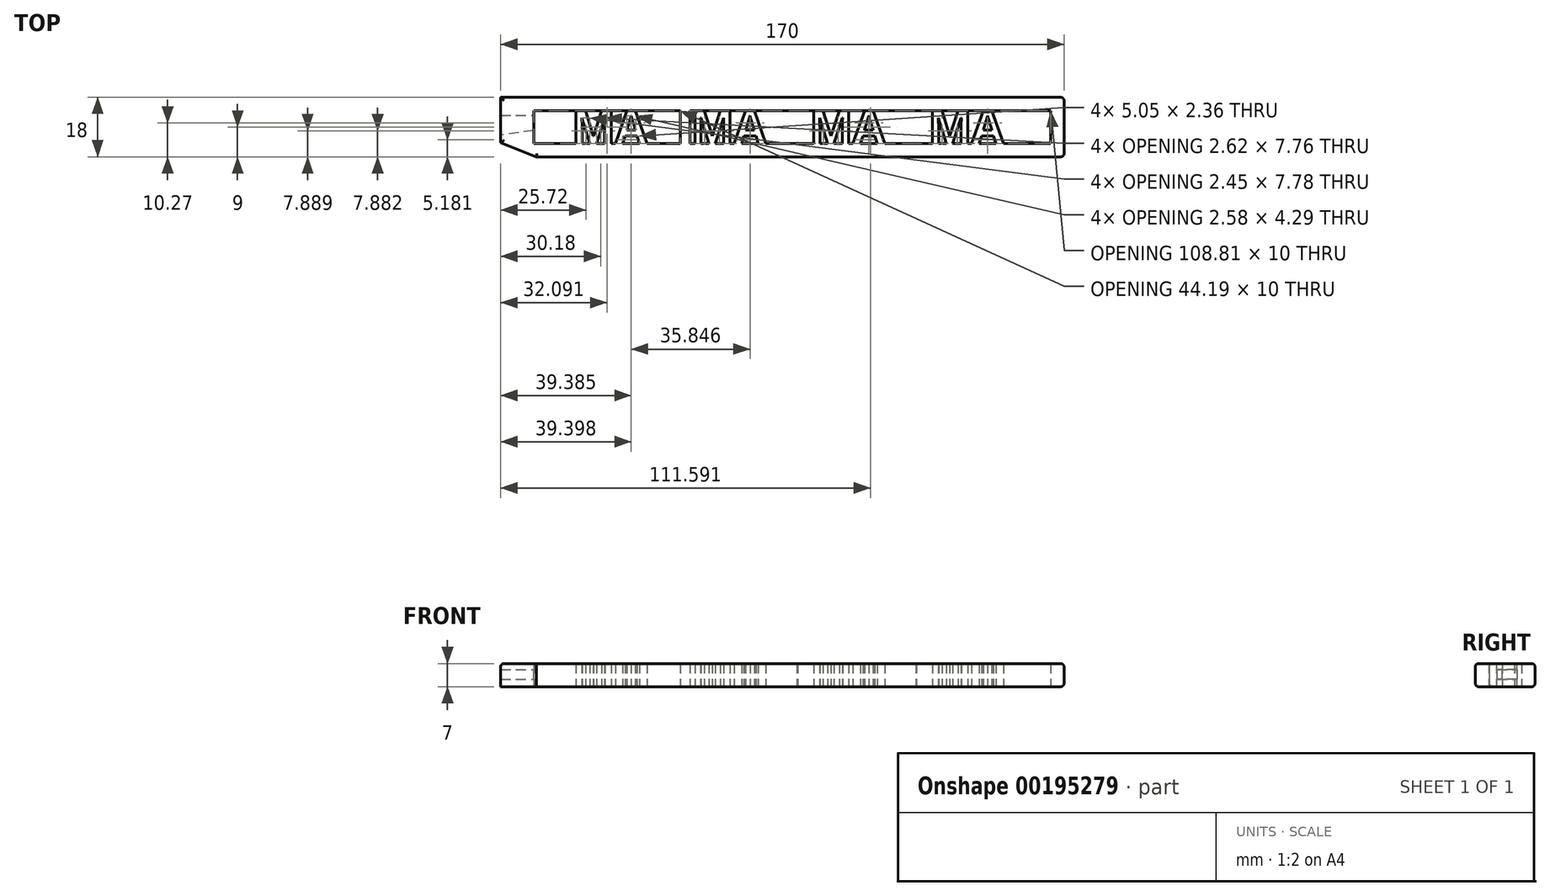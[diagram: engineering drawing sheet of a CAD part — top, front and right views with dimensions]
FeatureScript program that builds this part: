
annotation { "Feature Type Name" : "Feature", "Feature Type Description" : "" }
export const myFeature = defineFeature(function(context is Context, id is Id, definition is map)
    precondition{}
    {
        {
            var Q0;
            Q0=qCreatedBy(makeId("Top.planeOp"),FACE);
            var sketch = newSketch(context, id + "F0", { "sketchPlane" : qUnion([Q0])});
            skLineSegment(sketch, "E0.bottom", {"start": v(54.29, -9) * mm, "end": v(-115.71, -9) * mm});
            skLineSegment(sketch, "E0.top", {"start": v(54.29, 9) * mm, "end": v(-115.71, 9) * mm});
            skLineSegment(sketch, "E0.left", {"start": v(54.29, -9) * mm, "end": v(54.29, 9) * mm});
            skLineSegment(sketch, "E0.right", {"start": v(-115.71, -9) * mm, "end": v(-115.71, 9) * mm});
            skLineSegment(sketch, "E1.bottom", {"start": v(-105.71, 5) * mm, "end": v(50.29, 5) * mm});
            skLineSegment(sketch, "E1.top", {"start": v(-105.71, -5) * mm, "end": v(50.29, -5) * mm});
            skLineSegment(sketch, "E1.left", {"start": v(-105.71, 5) * mm, "end": v(-105.71, -5) * mm});
            skLineSegment(sketch, "E1.right", {"start": v(50.29, 5) * mm, "end": v(50.29, -5) * mm});
            skText(sketch, "E2", { "text": " MAX MAX MAX MAX ", "fontName": "OpenSans-Bold.ttf"});
            skLineSegment(sketch, "E3", {"start": v(-26.27, 5) * mm, "end": v(-26.27, -5) * mm});
            skLineSegment(sketch, "E4", {"start": v(-23.27, -5) * mm, "end": v(-23.27, 5) * mm});
            skLineSegment(sketch, "E5", {"start": v(9.6, 5) * mm, "end": v(9.6, -5) * mm});
            skLineSegment(sketch, "E6", {"start": v(12.6, 5) * mm, "end": v(12.6, -5) * mm});
            skLineSegment(sketch, "E7", {"start": v(-61.52, 5) * mm, "end": v(-61.52, -5) * mm});
            skLineSegment(sketch, "E8", {"start": v(-58.52, -5) * mm, "end": v(-58.52, 5) * mm});
            skPoint(sketch, "E9", {"position": v(-57.42, -2.4) * mm});
            skPoint(sketch, "E10", {"position": v(13.7, -2.4) * mm});
            const initialGuessF0  = {"E2": [-0.09782, -0.005, 1, 0, 0.01]};
            skSetInitialGuess(sketch, initialGuessF0);
            skSolve(sketch);
        }
        {
            var Q0;
            Q0=makeQuery(id+"F0.imprint","IMPRINT",FACE,{"disambiguationData":[TD([[makeQuery(id+"F0.imprint","IMPRINT",EDGE,{"derivedFrom":sQuery(id+"F0.wireOp",EDGE,"E0.bottom")}),-1.0]])]});
            var Q1;
            Q1=makeQuery(id+"F0.imprint","IMPRINT",FACE,{"disambiguationData":[TD([[makeQuery(id+"F0.imprint","IMPRINT",EDGE,{"derivedFrom":sQuery(id+"F0.wireOp",EDGE,"E2.sketch_text.stroke-0")}),-1.0]])]});
            var Q2;
            Q2=makeQuery(id+"F0.imprint","IMPRINT",FACE,{"disambiguationData":[TD([[makeQuery(id+"F0.imprint","IMPRINT",EDGE,{"derivedFrom":sQuery(id+"F0.wireOp",EDGE,"E2.sketch_text.stroke-19")}),-1.0]])]});
            var Q3;
            Q3=makeQuery(id+"F0.imprint","IMPRINT",FACE,{"disambiguationData":[TD([[makeQuery(id+"F0.imprint","IMPRINT",EDGE,{"derivedFrom":sQuery(id+"F0.wireOp",EDGE,"E2.sketch_text.stroke-31")}),-1.0]])]});
            var Q4;
            Q4=makeQuery(id+"F0.imprint","IMPRINT",FACE,{"disambiguationData":[TD([[makeQuery(id+"F0.imprint","IMPRINT",EDGE,{"derivedFrom":sQuery(id+"F0.wireOp",EDGE,"E2.sketch_text.stroke-43")}),-1.0]])]});
            var Q5;
            Q5=makeQuery(id+"F0.imprint","IMPRINT",FACE,{"disambiguationData":[TD([[makeQuery(id+"F0.imprint","IMPRINT",EDGE,{"derivedFrom":sQuery(id+"F0.wireOp",EDGE,"E2.sketch_text.stroke-62")}),-1.0]])]});
            var Q6;
            Q6=makeQuery(id+"F0.imprint","IMPRINT",FACE,{"disambiguationData":[TD([[makeQuery(id+"F0.imprint","IMPRINT",EDGE,{"derivedFrom":sQuery(id+"F0.wireOp",EDGE,"E2.sketch_text.stroke-74")}),-1.0]])]});
            var Q7;
            Q7=makeQuery(id+"F0.imprint","IMPRINT",FACE,{"disambiguationData":[TD([[makeQuery(id+"F0.imprint","IMPRINT",EDGE,{"derivedFrom":sQuery(id+"F0.wireOp",EDGE,"E2.sketch_text.stroke-86")}),-1.0]])]});
            var Q8;
            Q8=makeQuery(id+"F0.imprint","IMPRINT",FACE,{"disambiguationData":[TD([[makeQuery(id+"F0.imprint","IMPRINT",EDGE,{"derivedFrom":sQuery(id+"F0.wireOp",EDGE,"E2.sketch_text.stroke-105")}),-1.0]])]});
            var Q9;
            Q9=makeQuery(id+"F0.imprint","IMPRINT",FACE,{"disambiguationData":[TD([[makeQuery(id+"F0.imprint","IMPRINT",EDGE,{"derivedFrom":sQuery(id+"F0.wireOp",EDGE,"E2.sketch_text.stroke-117")}),-1.0]])]});
            var Q10;
            Q10=makeQuery(id+"F0.imprint","IMPRINT",FACE,{"disambiguationData":[TD([[makeQuery(id+"F0.imprint","IMPRINT",EDGE,{"derivedFrom":sQuery(id+"F0.wireOp",EDGE,"E2.sketch_text.stroke-129")}),-1.0]])]});
            var Q11;
            Q11=makeQuery(id+"F0.imprint","IMPRINT",FACE,{"disambiguationData":[TD([[makeQuery(id+"F0.imprint","IMPRINT",EDGE,{"derivedFrom":sQuery(id+"F0.wireOp",EDGE,"E2.sketch_text.stroke-148")}),-1.0]])]});
            var Q12;
            Q12=makeQuery(id+"F0.imprint","IMPRINT",FACE,{"disambiguationData":[TD([[makeQuery(id+"F0.imprint","IMPRINT",EDGE,{"derivedFrom":sQuery(id+"F0.wireOp",EDGE,"E2.sketch_text.stroke-160")}),-1.0]])]});
            var Q13;
            {var subQ0=sQuery(id+"F0.wireOp",EDGE,"E7");Q13=makeQuery(id+"F0.imprint","IMPRINT",FACE,{"disambiguationData":[TD([[makeQuery(id+"F0.imprint","IMPRINT",EDGE,{"derivedFrom":subQ0}),1.0]])]});}
            var Q14;
            {var subQ0=sQuery(id+"F0.wireOp",EDGE,"E3");Q14=makeQuery(id+"F0.imprint","IMPRINT",FACE,{"disambiguationData":[TD([[makeQuery(id+"F0.imprint","IMPRINT",EDGE,{"derivedFrom":subQ0}),1.0]])]});}
            var Q15;
            {var subQ0=sQuery(id+"F0.wireOp",EDGE,"E5");Q15=makeQuery(id+"F0.imprint","IMPRINT",FACE,{"disambiguationData":[TD([[makeQuery(id+"F0.imprint","IMPRINT",EDGE,{"derivedFrom":subQ0}),1.0]])]});}
            extrude(context, id + "F1", {"entities" : qUnion([Q0, Q1, Q2, Q3, Q4, Q5, Q6, Q7, Q8, Q9, Q10, Q11, Q12, Q13, Q14, Q15]), "endBound" : BoundingType.SYMMETRIC, "depth" : 7 * mm});
        }
        {
            var Q0;
            Q0=qCreatedBy(makeId("Top.planeOp"),FACE);
            var sketch = newSketch(context, id + "F2", { "sketchPlane" : qUnion([Q0])});
            skLineSegment(sketch, "E11", {"start": v(-116.71, 3.5) * mm, "end": v(-105.21, 3.5) * mm});
            skLineSegment(sketch, "E12", {"start": v(-105.21, -1) * mm, "end": v(-116.71, -2.5) * mm});
            skLineSegment(sketch, "E13", {"start": v(-105.21, 3.5) * mm, "end": v(-105.21, -1) * mm});
            skLineSegment(sketch, "E14", {"start": v(-116.71, 3.5) * mm, "end": v(-116.71, -2.5) * mm});
            skSolve(sketch);
        }
        {
            var Q0;
            Q0 = qSketchRegion(id + "F2", true);
            extrude(context, id + "F3", {"entities" : qUnion([Q0]), "operationType" : NewBodyOperationType.REMOVE, "depth" : 1.7 * mm, "hasSecondDirection" : true, "secondDirectionOppositeDirection" : true, "secondDirectionDepth" : 1.2 * mm});
        }
        {
            var Q0;
            Q0=qCreatedBy(makeId("Top.planeOp"),FACE);
            var sketch = newSketch(context, id + "F4", { "sketchPlane" : qUnion([Q0])});
            skLineSegment(sketch, "E15", {"start": v(-104.42, -9.2) * mm, "end": v(-117.77, -3.9) * mm});
            skLineSegment(sketch, "E16", {"start": v(-117.77, -3.9) * mm, "end": v(-117.77, -10.56) * mm});
            skLineSegment(sketch, "E17", {"start": v(-117.77, -10.56) * mm, "end": v(-104.42, -9.2) * mm});
            skSolve(sketch);
        }
        {
            var Q0;
            Q0 = qSketchRegion(id + "F4", true);
            extrude(context, id + "F5", {"entities" : qUnion([Q0]), "operationType" : NewBodyOperationType.REMOVE, "endBound" : BoundingType.SYMMETRIC, "depth" : 15 * mm});
        }
        {
            var Q0;
            Q0=makeQuery(id+"F1.opExtrude","CAP_EDGE",EDGE,{"disambiguationData":[OSD([sQuery(id+"F0.wireOp",EDGE,"E0.left")])],"isStart":true});
            var Q1;
            Q1=makeQuery(id+"F1.opExtrude","CAP_EDGE",EDGE,{"disambiguationData":[OSD([sQuery(id+"F0.wireOp",EDGE,"E0.top")])],"isStart":true});
            var Q2;
            Q2=makeQuery(id+"F1.opExtrude","CAP_EDGE",EDGE,{"disambiguationData":[OSD([sQuery(id+"F0.wireOp",EDGE,"E0.bottom")])],"isStart":true});
            var Q3;
            Q3=makeQuery(id+"F1.opExtrude","CAP_EDGE",EDGE,{"disambiguationData":[OSD([sQuery(id+"F0.wireOp",EDGE,"E0.left")])],"isStart":false});
            var Q4;
            Q4=makeQuery(id+"F1.opExtrude","SWEPT_EDGE",EDGE,{"disambiguationData":[OSD([sQuery(id+"F0.wireOp",EDGE,"E0.top"),sQuery(id+"F0.wireOp",EDGE,"E0.left")])]});
            var Q5;
            Q5=makeQuery(id+"F1.opExtrude","SWEPT_EDGE",EDGE,{"disambiguationData":[OSD([sQuery(id+"F0.wireOp",EDGE,"E0.bottom"),sQuery(id+"F0.wireOp",EDGE,"E0.left")])]});
            var Q6;
            Q6=makeQuery(id+"F5.boolean.opBoolean","INTERSECT",EDGE,{"derivedFrom":[makeQuery(id+"F1.opExtrude","CAP_FACE",FACE,{"disambiguationData":[OSD([sQuery(id+"F0.wireOp",EDGE,"E0.bottom"),sQuery(id+"F0.wireOp",EDGE,"E0.top"),sQuery(id+"F0.wireOp",EDGE,"E0.left"),sQuery(id+"F0.wireOp",EDGE,"E0.right"),sQuery(id+"F0.wireOp",EDGE,"E1.bottom"),sQuery(id+"F0.wireOp",EDGE,"E1.top"),sQuery(id+"F0.wireOp",EDGE,"E1.left"),sQuery(id+"F0.wireOp",EDGE,"E1.right"),sQuery(id+"F0.wireOp",EDGE,"E2.sketch_text.stroke-0"),sQuery(id+"F0.wireOp",EDGE,"E2.sketch_text.stroke-1"),sQuery(id+"F0.wireOp",EDGE,"E2.sketch_text.stroke-2"),sQuery(id+"F0.wireOp",EDGE,"E2.sketch_text.stroke-3"),sQuery(id+"F0.wireOp",EDGE,"E2.sketch_text.stroke-5"),sQuery(id+"F0.wireOp",EDGE,"E2.sketch_text.stroke-6"),sQuery(id+"F0.wireOp",EDGE,"E2.sketch_text.stroke-7"),sQuery(id+"F0.wireOp",EDGE,"E2.sketch_text.stroke-8"),sQuery(id+"F0.wireOp",EDGE,"E2.sketch_text.stroke-9"),sQuery(id+"F0.wireOp",EDGE,"E2.sketch_text.stroke-10"),sQuery(id+"F0.wireOp",EDGE,"E2.sketch_text.stroke-11"),sQuery(id+"F0.wireOp",EDGE,"E2.sketch_text.stroke-13"),sQuery(id+"F0.wireOp",EDGE,"E2.sketch_text.stroke-14"),sQuery(id+"F0.wireOp",EDGE,"E2.sketch_text.stroke-15"),sQuery(id+"F0.wireOp",EDGE,"E2.sketch_text.stroke-16"),sQuery(id+"F0.wireOp",EDGE,"E2.sketch_text.stroke-17"),sQuery(id+"F0.wireOp",EDGE,"E2.sketch_text.stroke-19"),sQuery(id+"F0.wireOp",EDGE,"E2.sketch_text.stroke-20"),sQuery(id+"F0.wireOp",EDGE,"E2.sketch_text.stroke-21"),sQuery(id+"F0.wireOp",EDGE,"E2.sketch_text.stroke-23"),sQuery(id+"F0.wireOp",EDGE,"E2.sketch_text.stroke-24"),sQuery(id+"F0.wireOp",EDGE,"E2.sketch_text.stroke-25"),sQuery(id+"F0.wireOp",EDGE,"E2.sketch_text.stroke-27"),sQuery(id+"F0.wireOp",EDGE,"E2.sketch_text.stroke-28"),sQuery(id+"F0.wireOp",EDGE,"E2.sketch_text.stroke-29"),sQuery(id+"F0.wireOp",EDGE,"E2.sketch_text.stroke-30"),sQuery(id+"F0.wireOp",EDGE,"E2.sketch_text.stroke-32"),sQuery(id+"F0.wireOp",EDGE,"E2.sketch_text.stroke-33"),sQuery(id+"F0.wireOp",EDGE,"E2.sketch_text.stroke-35"),sQuery(id+"F0.wireOp",EDGE,"E2.sketch_text.stroke-36"),sQuery(id+"F0.wireOp",EDGE,"E2.sketch_text.stroke-37"),sQuery(id+"F0.wireOp",EDGE,"E2.sketch_text.stroke-38"),sQuery(id+"F0.wireOp",EDGE,"E2.sketch_text.stroke-39"),sQuery(id+"F0.wireOp",EDGE,"E2.sketch_text.stroke-40"),sQuery(id+"F0.wireOp",EDGE,"E2.sketch_text.stroke-41"),sQuery(id+"F0.wireOp",EDGE,"E2.sketch_text.stroke-42"),sQuery(id+"F0.wireOp",EDGE,"E2.sketch_text.stroke-43"),sQuery(id+"F0.wireOp",EDGE,"E2.sketch_text.stroke-44"),sQuery(id+"F0.wireOp",EDGE,"E2.sketch_text.stroke-45"),sQuery(id+"F0.wireOp",EDGE,"E2.sketch_text.stroke-46"),sQuery(id+"F0.wireOp",EDGE,"E2.sketch_text.stroke-48"),sQuery(id+"F0.wireOp",EDGE,"E2.sketch_text.stroke-49"),sQuery(id+"F0.wireOp",EDGE,"E2.sketch_text.stroke-50"),sQuery(id+"F0.wireOp",EDGE,"E2.sketch_text.stroke-51"),sQuery(id+"F0.wireOp",EDGE,"E2.sketch_text.stroke-52"),sQuery(id+"F0.wireOp",EDGE,"E2.sketch_text.stroke-53"),sQuery(id+"F0.wireOp",EDGE,"E2.sketch_text.stroke-54"),sQuery(id+"F0.wireOp",EDGE,"E2.sketch_text.stroke-56"),sQuery(id+"F0.wireOp",EDGE,"E2.sketch_text.stroke-57"),sQuery(id+"F0.wireOp",EDGE,"E2.sketch_text.stroke-58"),sQuery(id+"F0.wireOp",EDGE,"E2.sketch_text.stroke-59"),sQuery(id+"F0.wireOp",EDGE,"E2.sketch_text.stroke-60"),sQuery(id+"F0.wireOp",EDGE,"E2.sketch_text.stroke-62"),sQuery(id+"F0.wireOp",EDGE,"E2.sketch_text.stroke-63"),sQuery(id+"F0.wireOp",EDGE,"E2.sketch_text.stroke-64"),sQuery(id+"F0.wireOp",EDGE,"E2.sketch_text.stroke-66"),sQuery(id+"F0.wireOp",EDGE,"E2.sketch_text.stroke-67"),sQuery(id+"F0.wireOp",EDGE,"E2.sketch_text.stroke-68"),sQuery(id+"F0.wireOp",EDGE,"E2.sketch_text.stroke-70"),sQuery(id+"F0.wireOp",EDGE,"E2.sketch_text.stroke-71"),sQuery(id+"F0.wireOp",EDGE,"E2.sketch_text.stroke-72"),sQuery(id+"F0.wireOp",EDGE,"E2.sketch_text.stroke-73"),sQuery(id+"F0.wireOp",EDGE,"E2.sketch_text.stroke-75"),sQuery(id+"F0.wireOp",EDGE,"E2.sketch_text.stroke-76"),sQuery(id+"F0.wireOp",EDGE,"E2.sketch_text.stroke-78"),sQuery(id+"F0.wireOp",EDGE,"E2.sketch_text.stroke-79"),sQuery(id+"F0.wireOp",EDGE,"E2.sketch_text.stroke-80"),sQuery(id+"F0.wireOp",EDGE,"E2.sketch_text.stroke-81"),sQuery(id+"F0.wireOp",EDGE,"E2.sketch_text.stroke-82"),sQuery(id+"F0.wireOp",EDGE,"E2.sketch_text.stroke-83"),sQuery(id+"F0.wireOp",EDGE,"E2.sketch_text.stroke-84"),sQuery(id+"F0.wireOp",EDGE,"E2.sketch_text.stroke-85"),sQuery(id+"F0.wireOp",EDGE,"E2.sketch_text.stroke-86"),sQuery(id+"F0.wireOp",EDGE,"E2.sketch_text.stroke-87"),sQuery(id+"F0.wireOp",EDGE,"E2.sketch_text.stroke-88"),sQuery(id+"F0.wireOp",EDGE,"E2.sketch_text.stroke-89"),sQuery(id+"F0.wireOp",EDGE,"E2.sketch_text.stroke-91"),sQuery(id+"F0.wireOp",EDGE,"E2.sketch_text.stroke-92"),sQuery(id+"F0.wireOp",EDGE,"E2.sketch_text.stroke-93"),sQuery(id+"F0.wireOp",EDGE,"E2.sketch_text.stroke-94"),sQuery(id+"F0.wireOp",EDGE,"E2.sketch_text.stroke-95"),sQuery(id+"F0.wireOp",EDGE,"E2.sketch_text.stroke-96"),sQuery(id+"F0.wireOp",EDGE,"E2.sketch_text.stroke-97"),sQuery(id+"F0.wireOp",EDGE,"E2.sketch_text.stroke-99"),sQuery(id+"F0.wireOp",EDGE,"E2.sketch_text.stroke-100"),sQuery(id+"F0.wireOp",EDGE,"E2.sketch_text.stroke-101"),sQuery(id+"F0.wireOp",EDGE,"E2.sketch_text.stroke-102"),sQuery(id+"F0.wireOp",EDGE,"E2.sketch_text.stroke-103"),sQuery(id+"F0.wireOp",EDGE,"E2.sketch_text.stroke-105"),sQuery(id+"F0.wireOp",EDGE,"E2.sketch_text.stroke-106"),sQuery(id+"F0.wireOp",EDGE,"E2.sketch_text.stroke-107"),sQuery(id+"F0.wireOp",EDGE,"E2.sketch_text.stroke-109"),sQuery(id+"F0.wireOp",EDGE,"E2.sketch_text.stroke-110"),sQuery(id+"F0.wireOp",EDGE,"E2.sketch_text.stroke-111"),sQuery(id+"F0.wireOp",EDGE,"E2.sketch_text.stroke-113"),sQuery(id+"F0.wireOp",EDGE,"E2.sketch_text.stroke-114"),sQuery(id+"F0.wireOp",EDGE,"E2.sketch_text.stroke-115"),sQuery(id+"F0.wireOp",EDGE,"E2.sketch_text.stroke-116"),sQuery(id+"F0.wireOp",EDGE,"E2.sketch_text.stroke-118"),sQuery(id+"F0.wireOp",EDGE,"E2.sketch_text.stroke-119"),sQuery(id+"F0.wireOp",EDGE,"E2.sketch_text.stroke-121"),sQuery(id+"F0.wireOp",EDGE,"E2.sketch_text.stroke-122"),sQuery(id+"F0.wireOp",EDGE,"E2.sketch_text.stroke-123"),sQuery(id+"F0.wireOp",EDGE,"E2.sketch_text.stroke-124"),sQuery(id+"F0.wireOp",EDGE,"E2.sketch_text.stroke-125"),sQuery(id+"F0.wireOp",EDGE,"E2.sketch_text.stroke-126"),sQuery(id+"F0.wireOp",EDGE,"E2.sketch_text.stroke-127"),sQuery(id+"F0.wireOp",EDGE,"E2.sketch_text.stroke-128"),sQuery(id+"F0.wireOp",EDGE,"E2.sketch_text.stroke-129"),sQuery(id+"F0.wireOp",EDGE,"E2.sketch_text.stroke-130"),sQuery(id+"F0.wireOp",EDGE,"E2.sketch_text.stroke-131"),sQuery(id+"F0.wireOp",EDGE,"E2.sketch_text.stroke-132"),sQuery(id+"F0.wireOp",EDGE,"E2.sketch_text.stroke-134"),sQuery(id+"F0.wireOp",EDGE,"E2.sketch_text.stroke-135"),sQuery(id+"F0.wireOp",EDGE,"E2.sketch_text.stroke-136"),sQuery(id+"F0.wireOp",EDGE,"E2.sketch_text.stroke-137"),sQuery(id+"F0.wireOp",EDGE,"E2.sketch_text.stroke-138"),sQuery(id+"F0.wireOp",EDGE,"E2.sketch_text.stroke-139"),sQuery(id+"F0.wireOp",EDGE,"E2.sketch_text.stroke-140"),sQuery(id+"F0.wireOp",EDGE,"E2.sketch_text.stroke-142"),sQuery(id+"F0.wireOp",EDGE,"E2.sketch_text.stroke-143"),sQuery(id+"F0.wireOp",EDGE,"E2.sketch_text.stroke-144"),sQuery(id+"F0.wireOp",EDGE,"E2.sketch_text.stroke-145"),sQuery(id+"F0.wireOp",EDGE,"E2.sketch_text.stroke-146"),sQuery(id+"F0.wireOp",EDGE,"E2.sketch_text.stroke-148"),sQuery(id+"F0.wireOp",EDGE,"E2.sketch_text.stroke-149"),sQuery(id+"F0.wireOp",EDGE,"E2.sketch_text.stroke-150"),sQuery(id+"F0.wireOp",EDGE,"E2.sketch_text.stroke-152"),sQuery(id+"F0.wireOp",EDGE,"E2.sketch_text.stroke-153"),sQuery(id+"F0.wireOp",EDGE,"E2.sketch_text.stroke-154"),sQuery(id+"F0.wireOp",EDGE,"E2.sketch_text.stroke-156"),sQuery(id+"F0.wireOp",EDGE,"E2.sketch_text.stroke-157"),sQuery(id+"F0.wireOp",EDGE,"E2.sketch_text.stroke-158"),sQuery(id+"F0.wireOp",EDGE,"E2.sketch_text.stroke-159"),sQuery(id+"F0.wireOp",EDGE,"E2.sketch_text.stroke-161"),sQuery(id+"F0.wireOp",EDGE,"E2.sketch_text.stroke-162"),sQuery(id+"F0.wireOp",EDGE,"E2.sketch_text.stroke-164"),sQuery(id+"F0.wireOp",EDGE,"E2.sketch_text.stroke-165"),sQuery(id+"F0.wireOp",EDGE,"E2.sketch_text.stroke-166"),sQuery(id+"F0.wireOp",EDGE,"E2.sketch_text.stroke-167"),sQuery(id+"F0.wireOp",EDGE,"E2.sketch_text.stroke-168"),sQuery(id+"F0.wireOp",EDGE,"E2.sketch_text.stroke-169"),sQuery(id+"F0.wireOp",EDGE,"E2.sketch_text.stroke-170"),sQuery(id+"F0.wireOp",EDGE,"E2.sketch_text.stroke-171")])],"isStart":true}),makeQuery(id+"F5.opExtrude","SWEPT_FACE",FACE,{"disambiguationData":[OSD([sQuery(id+"F4.wireOp",EDGE,"E15")])]})]});
            var Q7;
            Q7=makeQuery(id+"F1.opExtrude","CAP_EDGE",EDGE,{"disambiguationData":[OSD([sQuery(id+"F0.wireOp",EDGE,"E0.bottom")])],"isStart":false});
            var Q8;
            Q8=makeQuery(id+"F1.opExtrude","CAP_EDGE",EDGE,{"disambiguationData":[OSD([sQuery(id+"F0.wireOp",EDGE,"E0.top")])],"isStart":false});
            var Q9;
            Q9=makeQuery(id+"F1.opExtrude","CAP_EDGE",EDGE,{"disambiguationData":[OSD([sQuery(id+"F0.wireOp",EDGE,"E0.right")])],"isStart":false});
            var Q10;
            Q10=makeQuery(id+"F5.boolean.opBoolean","INTERSECT",EDGE,{"derivedFrom":[makeQuery(id+"F1.opExtrude","CAP_FACE",FACE,{"disambiguationData":[OSD([sQuery(id+"F0.wireOp",EDGE,"E0.bottom"),sQuery(id+"F0.wireOp",EDGE,"E0.top"),sQuery(id+"F0.wireOp",EDGE,"E0.left"),sQuery(id+"F0.wireOp",EDGE,"E0.right"),sQuery(id+"F0.wireOp",EDGE,"E1.bottom"),sQuery(id+"F0.wireOp",EDGE,"E1.top"),sQuery(id+"F0.wireOp",EDGE,"E1.left"),sQuery(id+"F0.wireOp",EDGE,"E1.right"),sQuery(id+"F0.wireOp",EDGE,"E2.sketch_text.stroke-0"),sQuery(id+"F0.wireOp",EDGE,"E2.sketch_text.stroke-1"),sQuery(id+"F0.wireOp",EDGE,"E2.sketch_text.stroke-2"),sQuery(id+"F0.wireOp",EDGE,"E2.sketch_text.stroke-3"),sQuery(id+"F0.wireOp",EDGE,"E2.sketch_text.stroke-5"),sQuery(id+"F0.wireOp",EDGE,"E2.sketch_text.stroke-6"),sQuery(id+"F0.wireOp",EDGE,"E2.sketch_text.stroke-7"),sQuery(id+"F0.wireOp",EDGE,"E2.sketch_text.stroke-8"),sQuery(id+"F0.wireOp",EDGE,"E2.sketch_text.stroke-9"),sQuery(id+"F0.wireOp",EDGE,"E2.sketch_text.stroke-10"),sQuery(id+"F0.wireOp",EDGE,"E2.sketch_text.stroke-11"),sQuery(id+"F0.wireOp",EDGE,"E2.sketch_text.stroke-13"),sQuery(id+"F0.wireOp",EDGE,"E2.sketch_text.stroke-14"),sQuery(id+"F0.wireOp",EDGE,"E2.sketch_text.stroke-15"),sQuery(id+"F0.wireOp",EDGE,"E2.sketch_text.stroke-16"),sQuery(id+"F0.wireOp",EDGE,"E2.sketch_text.stroke-17"),sQuery(id+"F0.wireOp",EDGE,"E2.sketch_text.stroke-19"),sQuery(id+"F0.wireOp",EDGE,"E2.sketch_text.stroke-20"),sQuery(id+"F0.wireOp",EDGE,"E2.sketch_text.stroke-21"),sQuery(id+"F0.wireOp",EDGE,"E2.sketch_text.stroke-23"),sQuery(id+"F0.wireOp",EDGE,"E2.sketch_text.stroke-24"),sQuery(id+"F0.wireOp",EDGE,"E2.sketch_text.stroke-25"),sQuery(id+"F0.wireOp",EDGE,"E2.sketch_text.stroke-27"),sQuery(id+"F0.wireOp",EDGE,"E2.sketch_text.stroke-28"),sQuery(id+"F0.wireOp",EDGE,"E2.sketch_text.stroke-29"),sQuery(id+"F0.wireOp",EDGE,"E2.sketch_text.stroke-30"),sQuery(id+"F0.wireOp",EDGE,"E2.sketch_text.stroke-32"),sQuery(id+"F0.wireOp",EDGE,"E2.sketch_text.stroke-33"),sQuery(id+"F0.wireOp",EDGE,"E2.sketch_text.stroke-35"),sQuery(id+"F0.wireOp",EDGE,"E2.sketch_text.stroke-36"),sQuery(id+"F0.wireOp",EDGE,"E2.sketch_text.stroke-37"),sQuery(id+"F0.wireOp",EDGE,"E2.sketch_text.stroke-38"),sQuery(id+"F0.wireOp",EDGE,"E2.sketch_text.stroke-39"),sQuery(id+"F0.wireOp",EDGE,"E2.sketch_text.stroke-40"),sQuery(id+"F0.wireOp",EDGE,"E2.sketch_text.stroke-41"),sQuery(id+"F0.wireOp",EDGE,"E2.sketch_text.stroke-42"),sQuery(id+"F0.wireOp",EDGE,"E2.sketch_text.stroke-43"),sQuery(id+"F0.wireOp",EDGE,"E2.sketch_text.stroke-44"),sQuery(id+"F0.wireOp",EDGE,"E2.sketch_text.stroke-45"),sQuery(id+"F0.wireOp",EDGE,"E2.sketch_text.stroke-46"),sQuery(id+"F0.wireOp",EDGE,"E2.sketch_text.stroke-48"),sQuery(id+"F0.wireOp",EDGE,"E2.sketch_text.stroke-49"),sQuery(id+"F0.wireOp",EDGE,"E2.sketch_text.stroke-50"),sQuery(id+"F0.wireOp",EDGE,"E2.sketch_text.stroke-51"),sQuery(id+"F0.wireOp",EDGE,"E2.sketch_text.stroke-52"),sQuery(id+"F0.wireOp",EDGE,"E2.sketch_text.stroke-53"),sQuery(id+"F0.wireOp",EDGE,"E2.sketch_text.stroke-54"),sQuery(id+"F0.wireOp",EDGE,"E2.sketch_text.stroke-56"),sQuery(id+"F0.wireOp",EDGE,"E2.sketch_text.stroke-57"),sQuery(id+"F0.wireOp",EDGE,"E2.sketch_text.stroke-58"),sQuery(id+"F0.wireOp",EDGE,"E2.sketch_text.stroke-59"),sQuery(id+"F0.wireOp",EDGE,"E2.sketch_text.stroke-60"),sQuery(id+"F0.wireOp",EDGE,"E2.sketch_text.stroke-62"),sQuery(id+"F0.wireOp",EDGE,"E2.sketch_text.stroke-63"),sQuery(id+"F0.wireOp",EDGE,"E2.sketch_text.stroke-64"),sQuery(id+"F0.wireOp",EDGE,"E2.sketch_text.stroke-66"),sQuery(id+"F0.wireOp",EDGE,"E2.sketch_text.stroke-67"),sQuery(id+"F0.wireOp",EDGE,"E2.sketch_text.stroke-68"),sQuery(id+"F0.wireOp",EDGE,"E2.sketch_text.stroke-70"),sQuery(id+"F0.wireOp",EDGE,"E2.sketch_text.stroke-71"),sQuery(id+"F0.wireOp",EDGE,"E2.sketch_text.stroke-72"),sQuery(id+"F0.wireOp",EDGE,"E2.sketch_text.stroke-73"),sQuery(id+"F0.wireOp",EDGE,"E2.sketch_text.stroke-75"),sQuery(id+"F0.wireOp",EDGE,"E2.sketch_text.stroke-76"),sQuery(id+"F0.wireOp",EDGE,"E2.sketch_text.stroke-78"),sQuery(id+"F0.wireOp",EDGE,"E2.sketch_text.stroke-79"),sQuery(id+"F0.wireOp",EDGE,"E2.sketch_text.stroke-80"),sQuery(id+"F0.wireOp",EDGE,"E2.sketch_text.stroke-81"),sQuery(id+"F0.wireOp",EDGE,"E2.sketch_text.stroke-82"),sQuery(id+"F0.wireOp",EDGE,"E2.sketch_text.stroke-83"),sQuery(id+"F0.wireOp",EDGE,"E2.sketch_text.stroke-84"),sQuery(id+"F0.wireOp",EDGE,"E2.sketch_text.stroke-85"),sQuery(id+"F0.wireOp",EDGE,"E2.sketch_text.stroke-86"),sQuery(id+"F0.wireOp",EDGE,"E2.sketch_text.stroke-87"),sQuery(id+"F0.wireOp",EDGE,"E2.sketch_text.stroke-88"),sQuery(id+"F0.wireOp",EDGE,"E2.sketch_text.stroke-89"),sQuery(id+"F0.wireOp",EDGE,"E2.sketch_text.stroke-91"),sQuery(id+"F0.wireOp",EDGE,"E2.sketch_text.stroke-92"),sQuery(id+"F0.wireOp",EDGE,"E2.sketch_text.stroke-93"),sQuery(id+"F0.wireOp",EDGE,"E2.sketch_text.stroke-94"),sQuery(id+"F0.wireOp",EDGE,"E2.sketch_text.stroke-95"),sQuery(id+"F0.wireOp",EDGE,"E2.sketch_text.stroke-96"),sQuery(id+"F0.wireOp",EDGE,"E2.sketch_text.stroke-97"),sQuery(id+"F0.wireOp",EDGE,"E2.sketch_text.stroke-99"),sQuery(id+"F0.wireOp",EDGE,"E2.sketch_text.stroke-100"),sQuery(id+"F0.wireOp",EDGE,"E2.sketch_text.stroke-101"),sQuery(id+"F0.wireOp",EDGE,"E2.sketch_text.stroke-102"),sQuery(id+"F0.wireOp",EDGE,"E2.sketch_text.stroke-103"),sQuery(id+"F0.wireOp",EDGE,"E2.sketch_text.stroke-105"),sQuery(id+"F0.wireOp",EDGE,"E2.sketch_text.stroke-106"),sQuery(id+"F0.wireOp",EDGE,"E2.sketch_text.stroke-107"),sQuery(id+"F0.wireOp",EDGE,"E2.sketch_text.stroke-109"),sQuery(id+"F0.wireOp",EDGE,"E2.sketch_text.stroke-110"),sQuery(id+"F0.wireOp",EDGE,"E2.sketch_text.stroke-111"),sQuery(id+"F0.wireOp",EDGE,"E2.sketch_text.stroke-113"),sQuery(id+"F0.wireOp",EDGE,"E2.sketch_text.stroke-114"),sQuery(id+"F0.wireOp",EDGE,"E2.sketch_text.stroke-115"),sQuery(id+"F0.wireOp",EDGE,"E2.sketch_text.stroke-116"),sQuery(id+"F0.wireOp",EDGE,"E2.sketch_text.stroke-118"),sQuery(id+"F0.wireOp",EDGE,"E2.sketch_text.stroke-119"),sQuery(id+"F0.wireOp",EDGE,"E2.sketch_text.stroke-121"),sQuery(id+"F0.wireOp",EDGE,"E2.sketch_text.stroke-122"),sQuery(id+"F0.wireOp",EDGE,"E2.sketch_text.stroke-123"),sQuery(id+"F0.wireOp",EDGE,"E2.sketch_text.stroke-124"),sQuery(id+"F0.wireOp",EDGE,"E2.sketch_text.stroke-125"),sQuery(id+"F0.wireOp",EDGE,"E2.sketch_text.stroke-126"),sQuery(id+"F0.wireOp",EDGE,"E2.sketch_text.stroke-127"),sQuery(id+"F0.wireOp",EDGE,"E2.sketch_text.stroke-128"),sQuery(id+"F0.wireOp",EDGE,"E2.sketch_text.stroke-129"),sQuery(id+"F0.wireOp",EDGE,"E2.sketch_text.stroke-130"),sQuery(id+"F0.wireOp",EDGE,"E2.sketch_text.stroke-131"),sQuery(id+"F0.wireOp",EDGE,"E2.sketch_text.stroke-132"),sQuery(id+"F0.wireOp",EDGE,"E2.sketch_text.stroke-134"),sQuery(id+"F0.wireOp",EDGE,"E2.sketch_text.stroke-135"),sQuery(id+"F0.wireOp",EDGE,"E2.sketch_text.stroke-136"),sQuery(id+"F0.wireOp",EDGE,"E2.sketch_text.stroke-137"),sQuery(id+"F0.wireOp",EDGE,"E2.sketch_text.stroke-138"),sQuery(id+"F0.wireOp",EDGE,"E2.sketch_text.stroke-139"),sQuery(id+"F0.wireOp",EDGE,"E2.sketch_text.stroke-140"),sQuery(id+"F0.wireOp",EDGE,"E2.sketch_text.stroke-142"),sQuery(id+"F0.wireOp",EDGE,"E2.sketch_text.stroke-143"),sQuery(id+"F0.wireOp",EDGE,"E2.sketch_text.stroke-144"),sQuery(id+"F0.wireOp",EDGE,"E2.sketch_text.stroke-145"),sQuery(id+"F0.wireOp",EDGE,"E2.sketch_text.stroke-146"),sQuery(id+"F0.wireOp",EDGE,"E2.sketch_text.stroke-148"),sQuery(id+"F0.wireOp",EDGE,"E2.sketch_text.stroke-149"),sQuery(id+"F0.wireOp",EDGE,"E2.sketch_text.stroke-150"),sQuery(id+"F0.wireOp",EDGE,"E2.sketch_text.stroke-152"),sQuery(id+"F0.wireOp",EDGE,"E2.sketch_text.stroke-153"),sQuery(id+"F0.wireOp",EDGE,"E2.sketch_text.stroke-154"),sQuery(id+"F0.wireOp",EDGE,"E2.sketch_text.stroke-156"),sQuery(id+"F0.wireOp",EDGE,"E2.sketch_text.stroke-157"),sQuery(id+"F0.wireOp",EDGE,"E2.sketch_text.stroke-158"),sQuery(id+"F0.wireOp",EDGE,"E2.sketch_text.stroke-159"),sQuery(id+"F0.wireOp",EDGE,"E2.sketch_text.stroke-161"),sQuery(id+"F0.wireOp",EDGE,"E2.sketch_text.stroke-162"),sQuery(id+"F0.wireOp",EDGE,"E2.sketch_text.stroke-164"),sQuery(id+"F0.wireOp",EDGE,"E2.sketch_text.stroke-165"),sQuery(id+"F0.wireOp",EDGE,"E2.sketch_text.stroke-166"),sQuery(id+"F0.wireOp",EDGE,"E2.sketch_text.stroke-167"),sQuery(id+"F0.wireOp",EDGE,"E2.sketch_text.stroke-168"),sQuery(id+"F0.wireOp",EDGE,"E2.sketch_text.stroke-169"),sQuery(id+"F0.wireOp",EDGE,"E2.sketch_text.stroke-170"),sQuery(id+"F0.wireOp",EDGE,"E2.sketch_text.stroke-171")])],"isStart":false}),makeQuery(id+"F5.opExtrude","SWEPT_FACE",FACE,{"disambiguationData":[OSD([sQuery(id+"F4.wireOp",EDGE,"E15")])]})]});
            fillet(context, id + "F6", {"entities" : qUnion([Q0, Q1, Q2, Q3, Q4, Q5, Q6, Q7, Q8, Q9, Q10]), "radius" : 1 * mm, "tangentPropagation" : true, "allowEdgeOverflow" : false});
        }
    });
